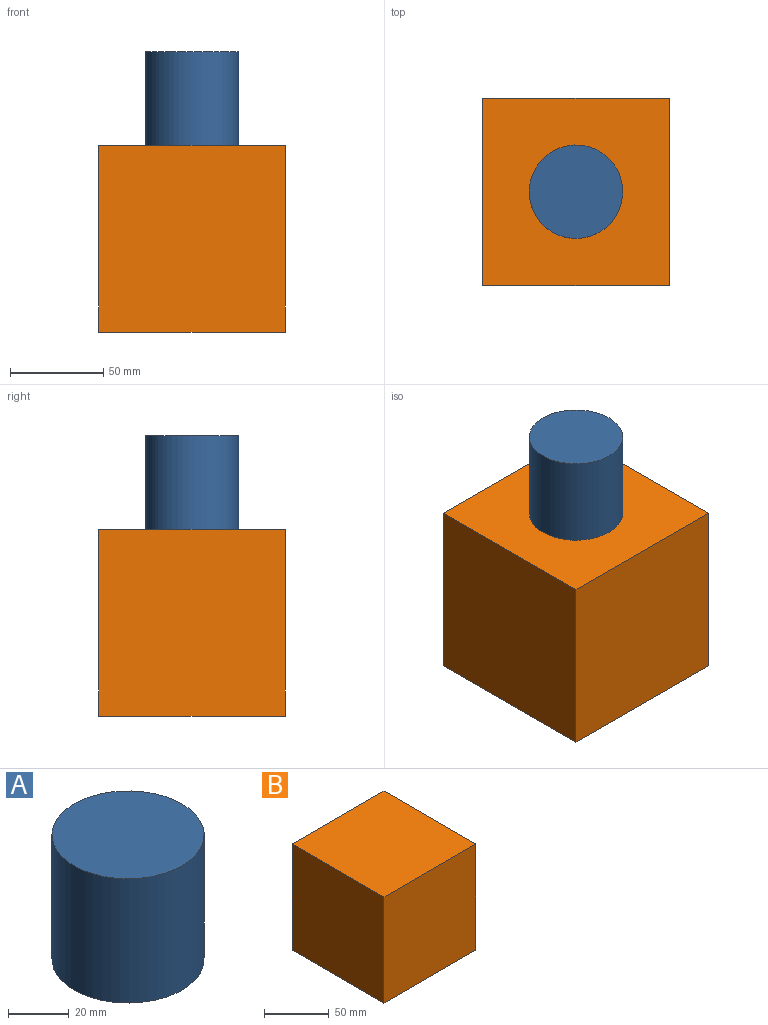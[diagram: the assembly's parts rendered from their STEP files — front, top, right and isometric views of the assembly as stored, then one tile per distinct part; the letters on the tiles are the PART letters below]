
ASSEMBLY  parts=2 mates=1
PART A: 3 faces, bbox 50x50x50 mm
  f0: cylinder r=25mm len=50mm, axis (0,0,-1), area 7854mm2, adj f1,f2
  f1: plane 50x50mm, normal (0,0,1), area 1963.5mm2, adj f0
  f2: plane 50x50mm, normal (0,0,-1), area 1963.5mm2, adj f0
PART B: 6 faces, bbox 100x100x100 mm
  f0: plane 100x100mm, normal (-1,0,0), area 10000mm2, adj f1,f3,f4,f5
  f1: plane 100x100mm, normal (0,-1,0), area 10000mm2, adj f0,f2,f4,f5
  f2: plane 100x100mm, normal (1,0,0), area 10000mm2, adj f1,f3,f4,f5
  f3: plane 100x100mm, normal (0,1,0), area 10000mm2, adj f0,f2,f4,f5
  f4: plane 100x100mm, normal (0,0,1), area 10000mm2, adj f0,f1,f2,f3
  f5: plane 100x100mm, normal (0,0,-1), area 10000mm2, adj f0,f1,f2,f3
PLACE A rot(axis=(1,0,0),180deg) t=(16.81,42.65,149.42)mm
PLACE B t=(-33.19,-7.35,-0.58)mm
MATE cylindrical A.f0 <-> B.f4  axis (0,0,-1) through (16.81,42.65,99.42)mm
